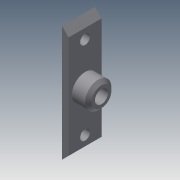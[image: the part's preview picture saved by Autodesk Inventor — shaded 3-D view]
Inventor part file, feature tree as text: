
AUTODESK INVENTOR PART (.ipt)
format: ipt  version: 2013 (Build 170138000, 138)  size: 107,008 bytes
history: native  units: mm
features: extrude x4, sketch x4, chamfer x2
ambient origin geometry x8: Origin, YZ Plane, XZ Plane, XY Plane, X Axis, Y Axis, Z Axis, Center Point
bodies: Solid1 (feature_tree)
feature tree (10):
  extrude  "Extrusion1"  Depth=10.0mm
  extrude  "Extrusion2"  Depth=8.0mm
  extrude  "Extrusion3"  Depth=4.0mm
  extrude  "Extrusion4"  Depth=5.0mm
  chamfer  "Chamfer1"  Distance=5.0mm
  chamfer  "Chamfer2"  Distance=3.0mm
  sketch  "Sketch1"  dims[d0=35.186mm d2=10.0mm]
  sketch  "Sketch2"  dims[d3=2.0mm d4=0.0mm d5=8.0mm]
  sketch  "Sketch3"  dims[d6=5.0mm d7=0.0mm d8=4.0mm]
  sketch  "Sketch4"  dims[d9=7.0mm d10=0.0mm d11=5.0mm d12=5.0mm d13=3.0mm d14=3.0mm d15=2.0mm d16=0.0mm d17=1.0mm d18=2.0mm d19=45.0deg d20=2.0mm d21=2.0mm d22=45.0deg]
